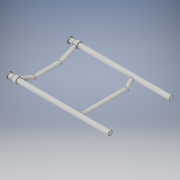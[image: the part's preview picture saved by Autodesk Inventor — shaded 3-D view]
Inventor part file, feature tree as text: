
AUTODESK INVENTOR PART (.ipt)
format: ipt  version: 2018 (Build 220112000, 112)  size: 158,720 bytes
history: native  units: in
note: dims shown in document units (in); Inventor stores cm internally (conversion verified against a paired STEP export)
features: sketch x7, extrude x3, sweep x2, plane x1
ambient origin geometry x8: Origin, YZ Plane, XZ Plane, XY Plane, X Axis, Y Axis, Z Axis, Center Point
bodies: Solid1 (feature_tree)
feature tree (13):
  sweep  "Sweep1"
  plane  "Work Plane1"
  sweep  "Sweep2"
  extrude  "Extrusion1"  TaperAngle=0.0deg  [1 undecoded]
  extrude  "Extrusion2"  Depth=15.0in
  extrude  "Extrusion3"  Depth=12.5in
  sketch  "Sketch1"  dims[d0=1.0in d1=3.5in]
  sketch  "Sketch2"  dims[d2=7.0in d3=16.25in]
  sketch  "Sketch3"  dims[d5=5.0in d6=0.0in d7=0.0in]
  sketch  "Sketch4"  dims[d8=15.0in d9=15.0in]
  sketch  "Sketch5"  dims[d10=1.0in d11=12.5in]
  sketch  "Sketch6"  dims[d13=0.0in]
  sketch  "Sketch7"  dims[d14=0.0in d15=0.0in d16=1.13in d17=25.0in d18=2.0in d19=0.0in d20=0.0in d21=1.56in d22=1.125in d23=0.0in d24=0.25in d25=0.0in d26=0.7719in]
note: 1 required parameter value undecoded (feature->parameter linkage not recoverable at this tier; creation-order binding heuristic only, values carry confidence <= 0.55)
